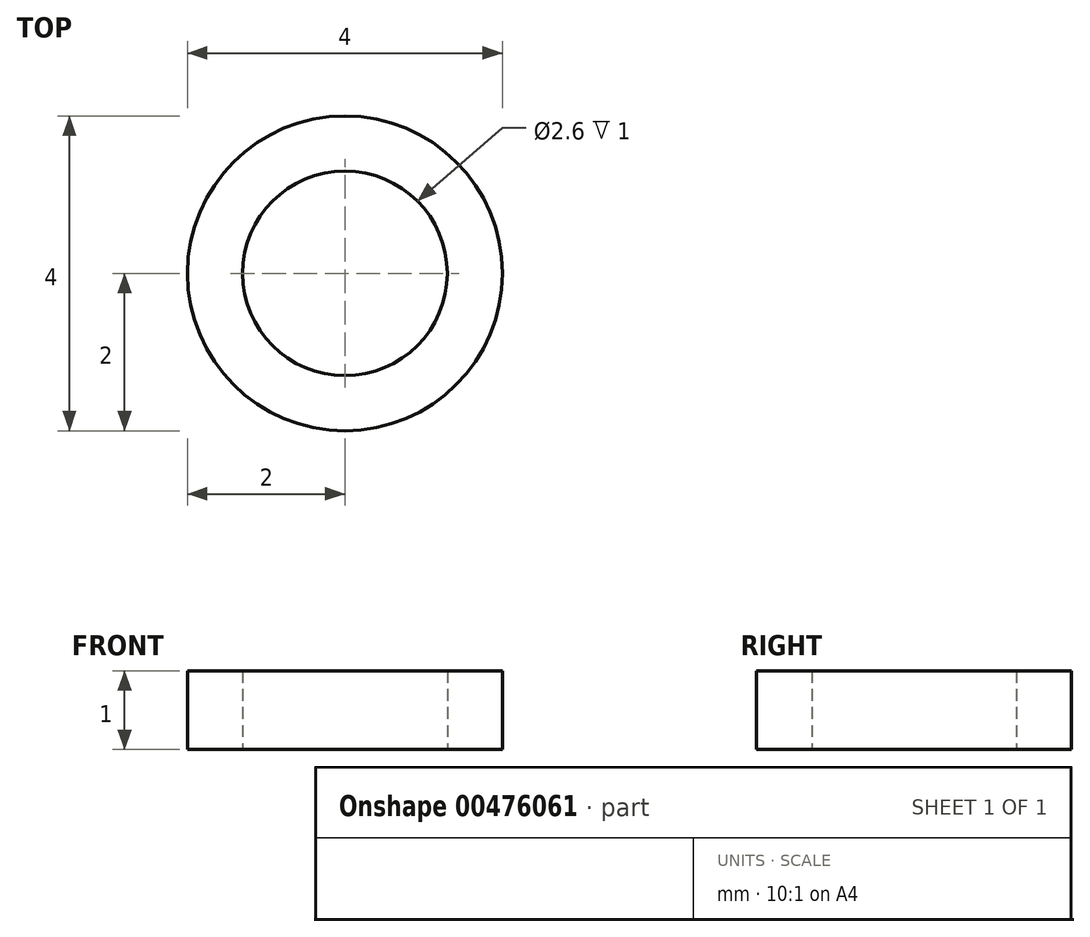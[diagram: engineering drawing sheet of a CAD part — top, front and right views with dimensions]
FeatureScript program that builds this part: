
annotation { "Feature Type Name" : "Feature", "Feature Type Description" : "" }
export const myFeature = defineFeature(function(context is Context, id is Id, definition is map)
    precondition{}
    {
        {
            var Q0;
            Q0=qCreatedBy(makeId("Top.planeOp"),FACE);
            var sketch = newSketch(context, id + "F0", { "sketchPlane" : qUnion([Q0])});
            skCircle(sketch, "E0", {"center": v(0, 0) * mm, "radius": 1.3 * mm});
            skCircle(sketch, "E1", {"center": v(0, 0) * mm, "radius": 2 * mm});
            skSolve(sketch);
        }
        {
            var Q0;
            Q0=makeQuery(id+"F0.imprint","IMPRINT",FACE,{"disambiguationData":[TD([[makeQuery(id+"F0.imprint","IMPRINT",EDGE,{"derivedFrom":sQuery(id+"F0.wireOp",EDGE,"E0")}),-1.0]])]});
            extrude(context, id + "F1", {"entities" : qUnion([Q0]), "depth" : 1 * mm});
        }
    });
